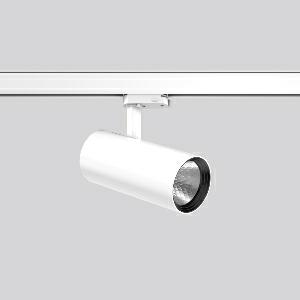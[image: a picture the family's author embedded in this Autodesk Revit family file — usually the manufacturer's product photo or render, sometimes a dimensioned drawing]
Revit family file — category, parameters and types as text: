
# Revit family: deecos_s_mini_742195_002_76_cbc4
name_source: partatom
category: Lighting Fixtures
units: mm (PartAtom-declared; Revit-internal decimal feet)

## family parameters
Cut with Voids When Loaded = No
Host = Face
Light Source = No
Part Type = Normal
Room Calculation Point = No
Round Connector Dimension = Use Diameter
Shared = No

## types (1)
- DEECOS S mini (1 x LED Modul 930, 2500 lm, 3000)
    Apparent Load = 20 VA
    Approval mark = CE
    CIE Flux Codes = 100 100 100 100 100
    Color Rendering = 90
    Color Temperature = 3000
    Default Elevation = 1800 mm
    Description = Series: DEECOS S mini
LED surface-mounted projector in modern design with no visible cooling ribs. Housing: die-cast aluminium, powder-coated. Rotation range: 356°. Swivel range: 90°. Black plastic ring and recessed LED to prevent glare from the side. Optical assembly with reflector made of MIRO-Silver with 98% total light reflection for outstanding efficiency - can be changed without tools. Best colour rendering index Ra>90. With adapter for RZB 3-circuit DALI tracks. Suitable for Track on ceiling, Wall track. High quality converter without flickering and stroboscopic effect. The following accessories can be mounted without use of tools: interchangeable lenses, decorative glasses, honeycomb louvre, clear and frosted diffusers, white interchangeable plastic ring. 
Colour: traffic white, matt (RAL 9016)
Diameter: 87 mm
Height: 214 mm
Lamp: LED
Socket: without socket
Colour temperature: 3000K
Colour rendering index (CRI): 92
System power: 20 W
Rated luminous flux: 2500 lm
Luminous efficiency: 125 lm/W
Control gear: Converter, dimmable, DALI
Protection class: I
Type of protection: IP 20
    Height = 214 mm
    Lamp = 1 x LED Modul 930
    Lamp Light Flux = 2500 lm
    Lamp count = 1
    Length = 87 mm
    Lifetime = 50000 h
    Luminous efficacy = 125 lm/W
    Manufacturer = RZB
    ModVariant = No
    Model = 742195.002.76
    Mounting Place = Ceiling
    Mounting Type = Rail mounted
    Number of Poles = 1
    OnlyDefault = Yes
    Power Factor = 1
    Product Name = DEECOS S mini
    Product group = Track mounted projectors
    ProductGroupID = 301
    Protection Class = Protection class I
    Protection Degree = IP 20
    RLX_Detail_Level = 1
    RLX_Emergency_Light_Flux = 0 lm
    RLX_Emergency_Type = 0
    RLX_Emergency_Type_DB = No
    RlxData = <blob elided: 35525 chars, md5=dce41474>
    Socket = socket
    Standby Power = 0 W
    System Light Flux = 2500 lm
    System Power = 20 W
    Type Comments = Product without accessories
    Type Image = 741926.002.jpg
    URL = http://relux.com
    VarID = ---
    Voltage = 230 V
    Voltage Range = 220-240 V
    Weight = 0.00 kg
    Width = 0 mm  [stored 0 ft]

note: [stored X ft] marks values corroborated as IEEE doubles in the binary element streams (Revit-internal decimal feet)

## geometry (parser evidence)
native form markers: Blend x4, Sweep x11
no freeform markers — native parametric forms only
